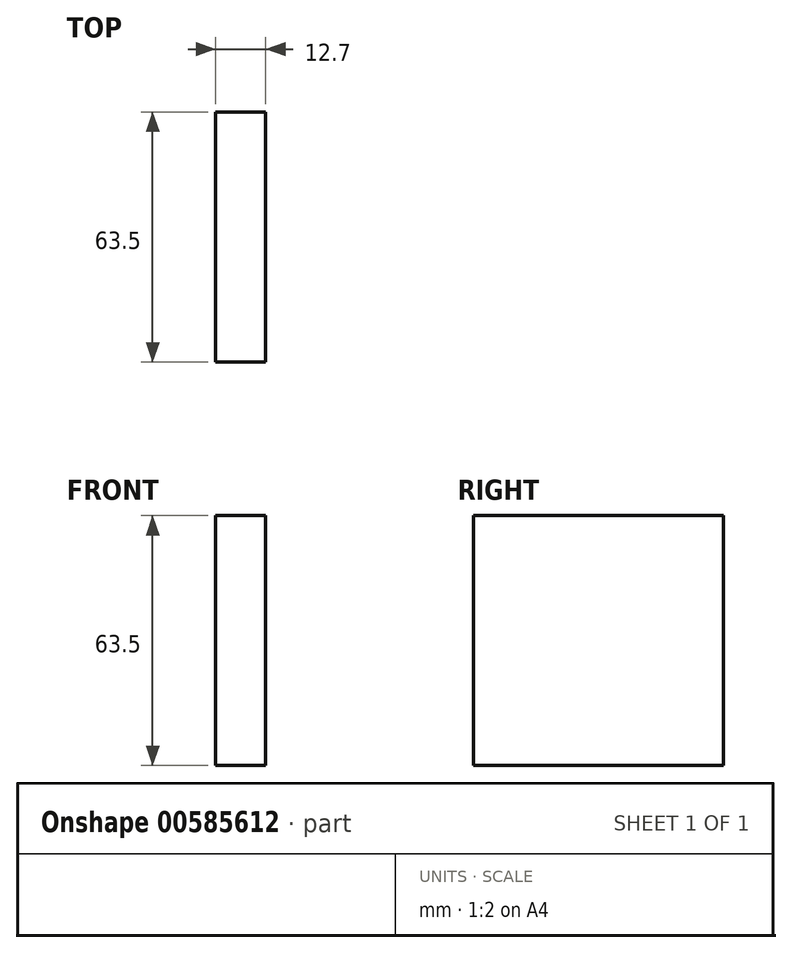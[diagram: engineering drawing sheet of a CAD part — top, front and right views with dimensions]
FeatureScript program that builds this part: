
annotation { "Feature Type Name" : "Feature", "Feature Type Description" : "" }
export const myFeature = defineFeature(function(context is Context, id is Id, definition is map)
    precondition{}
    {
        {
            var Q0;
            Q0=qCreatedBy(makeId("Top.planeOp"),FACE);
            var sketch = newSketch(context, id + "F0", { "sketchPlane" : qUnion([Q0])});
            skLineSegment(sketch, "E0.bottom", {"start": v(-6.35, 31.75) * mm, "end": v(6.35, 31.75) * mm});
            skLineSegment(sketch, "E0.top", {"start": v(-6.35, -31.75) * mm, "end": v(6.35, -31.75) * mm});
            skLineSegment(sketch, "E0.left", {"start": v(-6.35, 31.75) * mm, "end": v(-6.35, -31.75) * mm});
            skLineSegment(sketch, "E0.right", {"start": v(6.35, 31.75) * mm, "end": v(6.35, -31.75) * mm});
            skPoint(sketch, "E0.middle", {"position": v(0, 0) * mm});
            skSolve(sketch);
        }
        {
            var Q0;
            Q0=makeQuery(id+"F0.imprint","IMPRINT",FACE,{"disambiguationData":[TD([[makeQuery(id+"F0.imprint","IMPRINT",EDGE,{"derivedFrom":sQuery(id+"F0.wireOp",EDGE,"E0.bottom")}),-1.0]])]});
            extrude(context, id + "F1", {"entities" : qUnion([Q0]), "depth" : 63.5 * mm, "offsetDistance" : 25.4 * mm});
        }
    });
